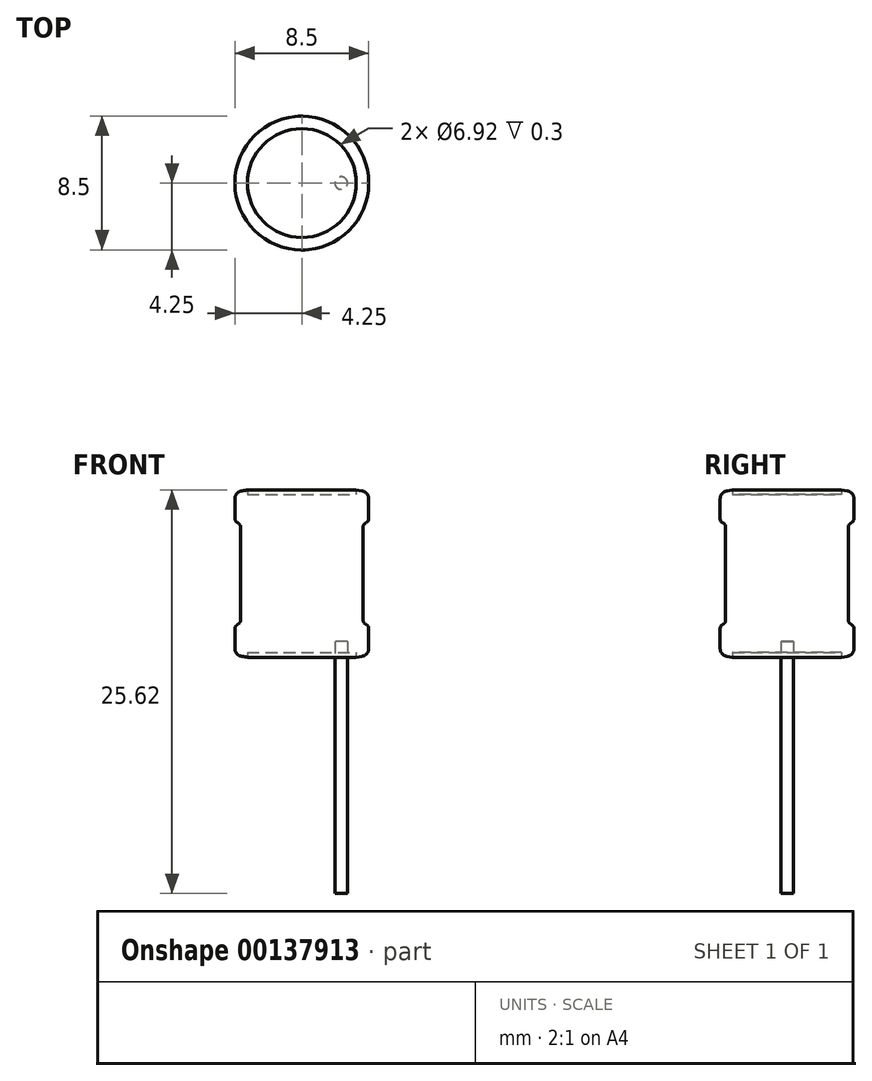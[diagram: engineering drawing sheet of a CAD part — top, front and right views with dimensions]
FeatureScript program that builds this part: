
annotation { "Feature Type Name" : "Feature", "Feature Type Description" : "" }
export const myFeature = defineFeature(function(context is Context, id is Id, definition is map)
    precondition{}
    {
        {
            var Q0;
            Q0=qCreatedBy(makeId("Front.planeOp"),FACE);
            var sketch = newSketch(context, id + "F0", { "sketchPlane" : qUnion([Q0])});
            skLineSegment(sketch, "E0", {"start": v(-3.46, 10.32) * mm, "end": v(-3.46, 10.62) * mm});
            skLineSegment(sketch, "E1", {"start": v(-3.9, 5.31) * mm, "end": v(-3.9, 8.3) * mm});
            skLineSegment(sketch, "E2", {"start": v(-4.25, 8.8) * mm, "end": v(-4.25, 10.07) * mm});
            skLineSegment(sketch, "E3", {"start": v(-3.46, 10.62) * mm, "end": v(-3.83, 10.56) * mm});
            skLineSegment(sketch, "E4", {"start": v(-3.46, 10.32) * mm, "end": v(0, 10.32) * mm});
            skPoint(sketch, "E5.visualSharp", {"position": v(-4.25, 10.5) * mm});
            skArc(sketch, "E5.filletArc", {"start": v(-3.83, 10.56) * mm, "mid": v(-4.13, 10.4) * mm, "end": v(-4.25, 10.07) * mm});
            skFitSpline(sketch, "E6", {"points": [v(-3.9, 8.3) * mm, v(-4.25, 8.8) * mm], "startDerivative": vector(0, 0.75) * mm, "endDerivative": vector(0, 0.83) * mm});
            skLineSegment(sketch, "E7", {"start": v(-3.9, 5.31) * mm, "end": v(0, 5.31) * mm});
            skLineSegment(sketch, "E8.MirrorCS", {"start": v(-3.9, 5.31) * mm, "end": v(-3.9, 2.32) * mm});
            skLineSegment(sketch, "E9.MirrorCS", {"start": v(-3.46, 0) * mm, "end": v(-3.83, 0.06) * mm});
            skLineSegment(sketch, "E10.MirrorCS", {"start": v(-3.46, 0.3) * mm, "end": v(-3.46, 0) * mm});
            skArc(sketch, "E11.MirrorCS", {"start": v(-3.83, 0.06) * mm, "mid": v(-4.13, 0.23) * mm, "end": v(-4.25, 0.55) * mm});
            skFitSpline(sketch, "E12.MirrorCS", {"points": [v(-3.9, 2.32) * mm, v(-4.25, 1.82) * mm], "startDerivative": vector(0, -0.75) * mm, "endDerivative": vector(0, -0.83) * mm});
            skLineSegment(sketch, "E13.MirrorCS", {"start": v(-3.46, 0.3) * mm, "end": v(0, 0.3) * mm});
            skLineSegment(sketch, "E14.MirrorCS", {"start": v(-4.25, 1.82) * mm, "end": v(-4.25, 0.55) * mm});
            skPoint(sketch, "E15.MirrorP", {"position": v(-4.25, 0.13) * mm});
            skFitSpline(sketch, "E16.MirrorCS", {"points": [v(3.9, 8.3) * mm, v(4.25, 8.8) * mm], "startDerivative": vector(0, 0.75) * mm, "endDerivative": vector(0, 0.83) * mm});
            skFitSpline(sketch, "E17.MirrorCS", {"points": [v(3.9, 2.32) * mm, v(4.25, 1.82) * mm], "startDerivative": vector(0, -0.75) * mm, "endDerivative": vector(0, -0.83) * mm});
            skLineSegment(sketch, "E18.MirrorCS", {"start": v(3.46, 10.62) * mm, "end": v(3.83, 10.56) * mm});
            skArc(sketch, "E19.MirrorCS", {"start": v(3.83, 0.06) * mm, "mid": v(4.13, 0.23) * mm, "end": v(4.25, 0.55) * mm});
            skLineSegment(sketch, "E20.MirrorCS", {"start": v(3.46, 0.3) * mm, "end": v(3.46, 0) * mm});
            skLineSegment(sketch, "E21.MirrorCS", {"start": v(3.46, 0) * mm, "end": v(3.83, 0.06) * mm});
            skLineSegment(sketch, "E22.MirrorCS", {"start": v(3.46, 10.32) * mm, "end": v(3.46, 10.62) * mm});
            skArc(sketch, "E23.MirrorCS", {"start": v(3.83, 10.56) * mm, "mid": v(4.13, 10.4) * mm, "end": v(4.25, 10.07) * mm});
            skLineSegment(sketch, "E24.MirrorCS", {"start": v(3.9, 5.31) * mm, "end": v(3.9, 2.32) * mm});
            skPoint(sketch, "E25.MirrorP", {"position": v(4.25, 10.5) * mm});
            skLineSegment(sketch, "E26.MirrorCS", {"start": v(4.25, 1.82) * mm, "end": v(4.25, 0.55) * mm});
            skPoint(sketch, "E27.MirrorP", {"position": v(4.25, 0.13) * mm});
            skLineSegment(sketch, "E28.MirrorCS", {"start": v(3.46, 10.32) * mm, "end": v(0, 10.32) * mm});
            skLineSegment(sketch, "E29.MirrorCS", {"start": v(3.9, 5.31) * mm, "end": v(3.9, 8.3) * mm});
            skLineSegment(sketch, "E30.MirrorCS", {"start": v(3.9, 5.31) * mm, "end": v(0, 5.31) * mm});
            skLineSegment(sketch, "E31.MirrorCS", {"start": v(4.25, 8.8) * mm, "end": v(4.25, 10.07) * mm});
            skLineSegment(sketch, "E32.MirrorCS", {"start": v(3.46, 0.3) * mm, "end": v(0, 0.3) * mm});
            skLineSegment(sketch, "E33", {"start": v(0, 10.32) * mm, "end": v(0, 5.31) * mm});
            skLineSegment(sketch, "E34", {"start": v(0, 5.31) * mm, "end": v(0, 0.3) * mm});
            skSolve(sketch);
        }
        {
            var Q0;
            Q0=qCreatedBy(makeId("Top.planeOp"),FACE);
            var sketch = newSketch(context, id + "F1", { "sketchPlane" : qUnion([Q0])});
            skLineSegment(sketch, "E35", {"start": v(0, 0) * mm, "end": v(2.5, 0) * mm});
            skCircle(sketch, "E36", {"center": v(2.5, 0) * mm, "radius": 0.4 * mm});
            skCircle(sketch, "E37.MirrorC", {"center": v(-2.5, 0) * mm, "radius": 0.4 * mm});
            skSolve(sketch);
        }
        {
            var Q0;
            Q0=makeQuery(id+"F1.imprint","IMPRINT",FACE,{"disambiguationData":[TD([[makeQuery(id+"F1.imprint","IMPRINT",EDGE,{"derivedFrom":sQuery(id+"F1.wireOp",EDGE,"E37.MirrorC")}),-1.0]])]});
            var Q1;
            Q1=makeQuery(id+"F1.imprint","IMPRINT",FACE,{"disambiguationData":[TD([[makeQuery(id+"F1.imprint","IMPRINT",EDGE,{"derivedFrom":sQuery(id+"F1.wireOp",EDGE,"E36")}),1.0]])]});
            extrude(context, id + "F2", {"entities" : qUnion([Q0, Q1]), "hasOffset" : true, "offsetDistance" : 10 * mm, "depth" : 1 * mm, "hasSecondDirection" : true, "secondDirectionOppositeDirection" : true, "hasSecondDirectionOffset" : true, "secondDirectionOffsetDistance" : 10 * mm, "secondDirectionOffsetOppositeDirection" : true, "secondDirectionDepth" : 15 * mm});
        }
        {
            var Q0;
            Q0=makeQuery(id+"F0.imprint","IMPRINT",FACE,{"disambiguationData":[TD([[makeQuery(id+"F0.imprint","IMPRINT",EDGE,{"derivedFrom":sQuery(id+"F0.wireOp",EDGE,"E16.MirrorCS")}),1.0]])]});
            var Q1;
            Q1=makeQuery(id+"F0.imprint","IMPRINT",FACE,{"disambiguationData":[TD([[makeQuery(id+"F0.imprint","IMPRINT",EDGE,{"derivedFrom":sQuery(id+"F0.wireOp",EDGE,"E17.MirrorCS")}),-1.0]])]});
            var Q2;
            Q2=sQuery(id+"F0.wireOp",EDGE,"E33");
            revolve(context, id + "F3", {"surfaceOperationType" : NewSurfaceOperationType.NEW, "entities" : qUnion([Q0, Q1]), "axis" : qUnion([Q2]), "revolveType" : RevolveType.FULL, "oppositeDirection" : true});
        }
    });
